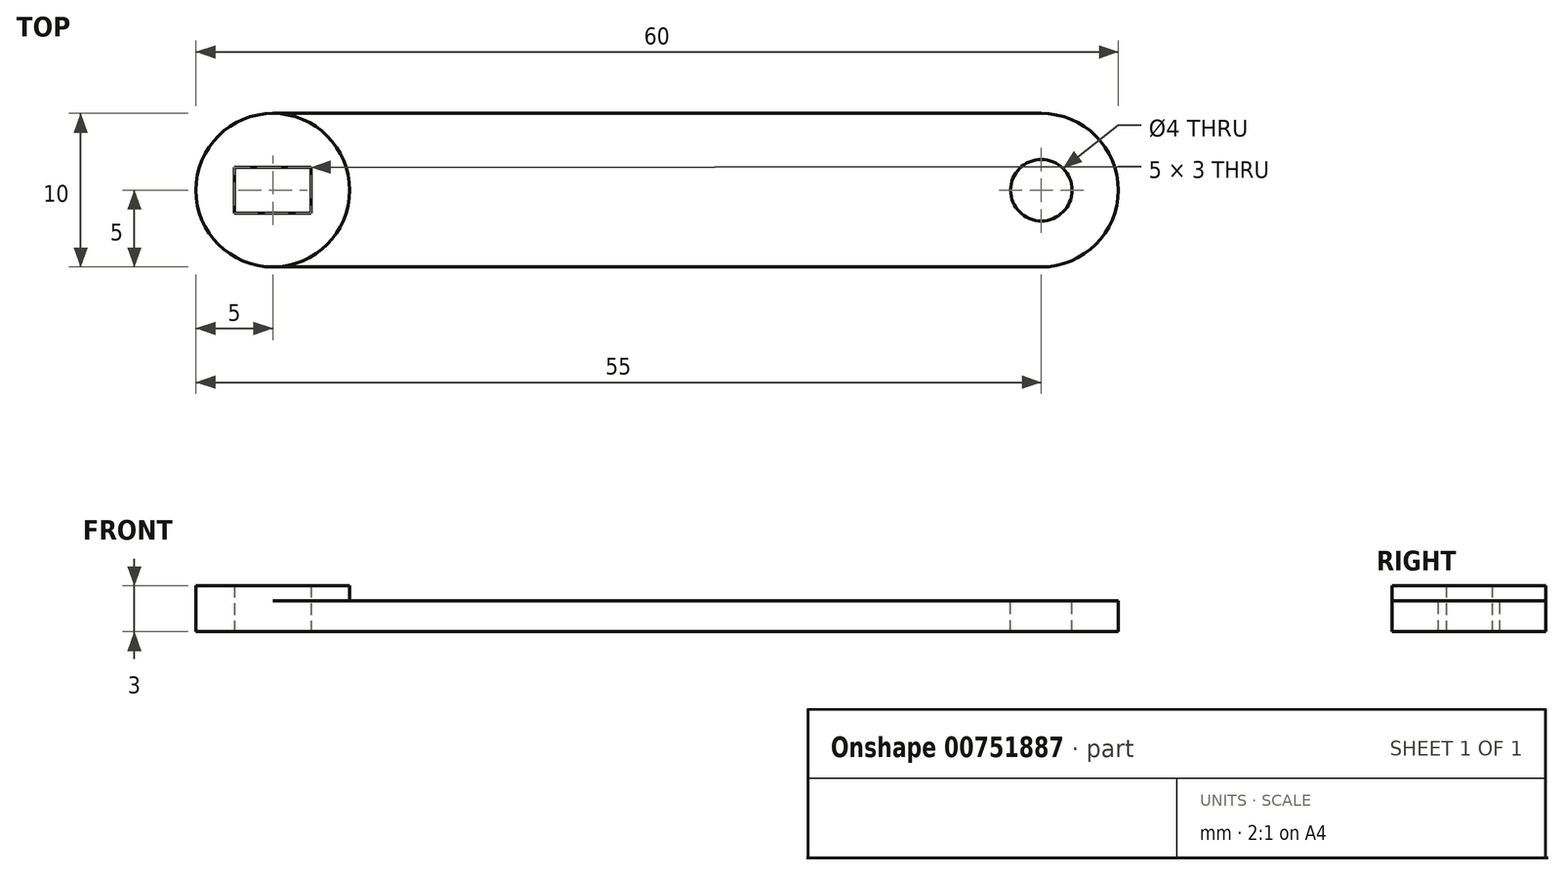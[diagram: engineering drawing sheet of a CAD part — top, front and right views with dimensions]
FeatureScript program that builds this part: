
annotation { "Feature Type Name" : "Feature", "Feature Type Description" : "" }
export const myFeature = defineFeature(function(context is Context, id is Id, definition is map)
    precondition{}
    {
        {
            var Q0;
            Q0=qCreatedBy(makeId("Top.planeOp"),FACE);
            var sketch = newSketch(context, id + "F0", { "sketchPlane" : qUnion([Q0])});
            skLineSegment(sketch, "E0.bottom", {"start": v(0, 0) * mm, "end": v(60, 0) * mm});
            skLineSegment(sketch, "E0.top", {"start": v(0, -10) * mm, "end": v(60, -10) * mm});
            skLineSegment(sketch, "E0.left", {"start": v(0, 0) * mm, "end": v(0, -10) * mm});
            skLineSegment(sketch, "E0.right", {"start": v(60, 0) * mm, "end": v(60, -10) * mm});
            skSolve(sketch);
        }
        {
            var Q0;
            Q0 = qSketchRegion(id + "F0", true);
            extrude(context, id + "F1", {"entities" : qUnion([Q0]), "depth" : 2 * mm, "offsetDistance" : 25 * mm});
        }
        {
            var Q0;
            Q0=makeQuery(id+"F1.opExtrude","SWEPT_EDGE",EDGE,{"disambiguationData":[OSD([sQuery(id+"F0.wireOp",EDGE,"E0.top"),sQuery(id+"F0.wireOp",EDGE,"E0.left")])]});
            var Q1;
            Q1=makeQuery(id+"F1.opExtrude","SWEPT_EDGE",EDGE,{"disambiguationData":[OSD([sQuery(id+"F0.wireOp",EDGE,"E0.bottom"),sQuery(id+"F0.wireOp",EDGE,"E0.left")])]});
            var Q2;
            Q2=makeQuery(id+"F1.opExtrude","SWEPT_EDGE",EDGE,{"disambiguationData":[OSD([sQuery(id+"F0.wireOp",EDGE,"E0.top"),sQuery(id+"F0.wireOp",EDGE,"E0.right")])]});
            var Q3;
            Q3=makeQuery(id+"F1.opExtrude","SWEPT_EDGE",EDGE,{"disambiguationData":[OSD([sQuery(id+"F0.wireOp",EDGE,"E0.bottom"),sQuery(id+"F0.wireOp",EDGE,"E0.right")])]});
            fillet(context, id + "F2", {"entities" : qUnion([Q0, Q1, Q2, Q3]), "radius" : 5 * mm, "tangentPropagation" : true, "allowEdgeOverflow" : false});
        }
        {
            var Q0;
            Q0=makeQuery(id+"F1.opExtrude","CAP_FACE",FACE,{"disambiguationData":[OSD([sQuery(id+"F0.wireOp",EDGE,"E0.bottom"),sQuery(id+"F0.wireOp",EDGE,"E0.top"),sQuery(id+"F0.wireOp",EDGE,"E0.left"),sQuery(id+"F0.wireOp",EDGE,"E0.right")])],"isStart":false});
            var sketch = newSketch(context, id + "F3", { "sketchPlane" : qUnion([Q0])});
            skCircle(sketch, "E1", {"center": v(5, -5) * mm, "radius": 5 * mm});
            skSolve(sketch);
        }
        {
            var Q0;
            Q0 = qSketchRegion(id + "F3", true);
            extrude(context, id + "F4", {"entities" : qUnion([Q0]), "operationType" : NewBodyOperationType.ADD, "depth" : 1 * mm, "offsetDistance" : 25 * mm});
        }
        {
            var Q0;
            Q0=makeQuery(id+"F1.opExtrude","CAP_FACE",FACE,{"disambiguationData":[OSD([sQuery(id+"F0.wireOp",EDGE,"E0.bottom"),sQuery(id+"F0.wireOp",EDGE,"E0.top"),sQuery(id+"F0.wireOp",EDGE,"E0.left"),sQuery(id+"F0.wireOp",EDGE,"E0.right")])],"isStart":false});
            var sketch = newSketch(context, id + "F5", { "sketchPlane" : qUnion([Q0])});
            skLineSegment(sketch, "E2.bottom", {"start": v(2.5, -3.5) * mm, "end": v(7.5, -3.5) * mm});
            skLineSegment(sketch, "E2.top", {"start": v(2.5, -6.5) * mm, "end": v(7.5, -6.5) * mm});
            skLineSegment(sketch, "E2.left", {"start": v(2.5, -3.5) * mm, "end": v(2.5, -6.5) * mm});
            skLineSegment(sketch, "E2.right", {"start": v(7.5, -3.5) * mm, "end": v(7.5, -6.5) * mm});
            skSolve(sketch);
        }
        {
            var Q0;
            Q0 = qSketchRegion(id + "F5", true);
            extrude(context, id + "F6", {"entities" : qUnion([Q0]), "operationType" : NewBodyOperationType.REMOVE, "endBound" : BoundingType.THROUGH_ALL, "depth" : 25 * mm, "offsetDistance" : 25 * mm, "hasSecondDirection" : true, "secondDirectionBound" : SecondDirectionBoundingType.THROUGH_ALL, "secondDirectionOppositeDirection" : true, "secondDirectionDepth" : 25 * mm});
        }
        {
            var Q0;
            Q0=makeQuery(id+"F1.opExtrude","CAP_FACE",FACE,{"disambiguationData":[OSD([sQuery(id+"F0.wireOp",EDGE,"E0.bottom"),sQuery(id+"F0.wireOp",EDGE,"E0.top"),sQuery(id+"F0.wireOp",EDGE,"E0.left"),sQuery(id+"F0.wireOp",EDGE,"E0.right")])],"isStart":false});
            var sketch = newSketch(context, id + "F7", { "sketchPlane" : qUnion([Q0])});
            skCircle(sketch, "E3", {"center": v(55, -5) * mm, "radius": 2 * mm});
            skSolve(sketch);
        }
        {
            var Q0;
            Q0 = qSketchRegion(id + "F7", true);
            extrude(context, id + "F8", {"entities" : qUnion([Q0]), "operationType" : NewBodyOperationType.REMOVE, "endBound" : BoundingType.THROUGH_ALL, "oppositeDirection" : true, "depth" : 25 * mm, "offsetDistance" : 25 * mm});
        }
    });
